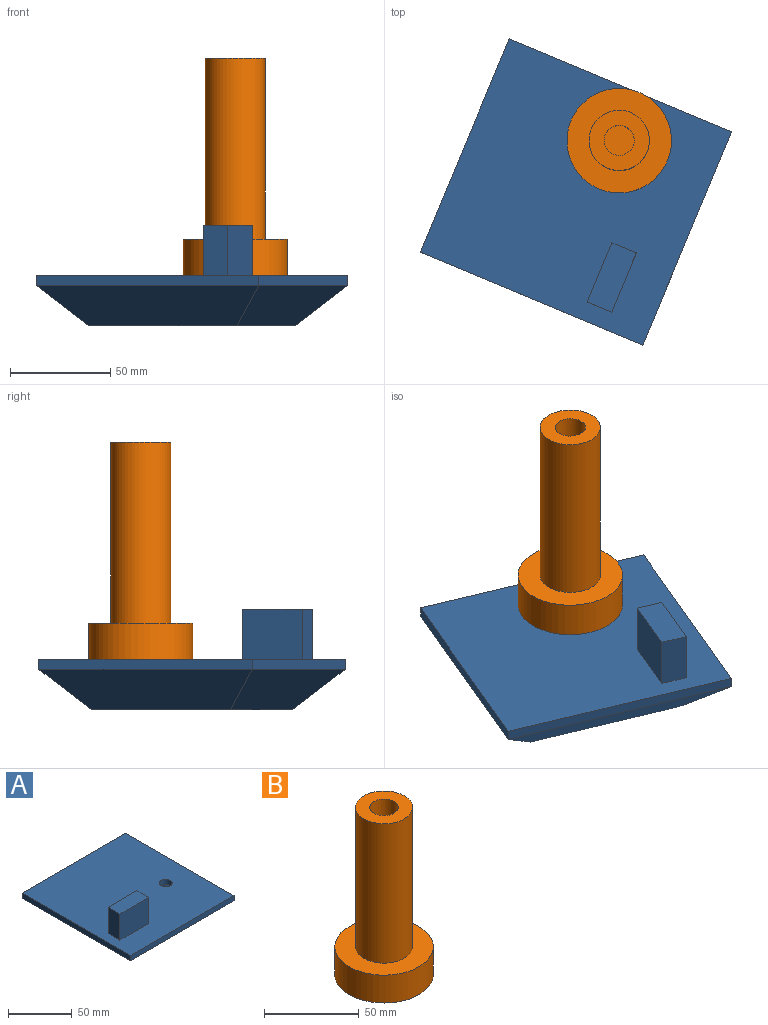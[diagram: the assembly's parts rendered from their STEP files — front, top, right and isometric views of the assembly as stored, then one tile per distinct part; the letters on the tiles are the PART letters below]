
ASSEMBLY  parts=2 mates=2
PART A: 17 faces, bbox 115x120x50 mm
  f0: plane 120x5mm, normal (-1,0,0), area 600mm2, adj f1,f4,f5,f12
  f1: plane 115x5mm, normal (0,-1,0), area 575mm2, adj f0,f2,f5,f15
  f2: plane 120x5mm, normal (1,0,0), area 600mm2, adj f1,f4,f5,f16
  f3: cylinder r=5mm len=10mm, axis (0,0,-1), area 157.1mm2, adj f5,f14
  f4: plane 115x5mm, normal (0,1,0), area 575mm2, adj f0,f2,f5,f13
  f5: plane 120x115mm, normal (0,0,1), area 13302.1mm2, adj f0,f1,f2,f3,f4,f7,f8,f9
  f6: plane 80x75mm, normal (0,0,-1), area 4736.5mm2, adj f12,f13,f14,f15,f16
  f7: plane 25x13.14mm, normal (-1,0,0), area 328.6mm2, adj f5,f8,f10,f11
  f8: plane 31.91x25mm, normal (0,-1,0), area 797.7mm2, adj f5,f7,f9,f11
  f9: plane 25x13.14mm, normal (1,0,0), area 328.6mm2, adj f5,f8,f10,f11
  f10: plane 31.91x25mm, normal (0,1,0), area 797.7mm2, adj f5,f7,f9,f11
  f11: plane 31.91x13.14mm, normal (0,0,1), area 419.3mm2, adj f7,f8,f9,f10
  f12: plane 120x20mm, normal (-0.71,0,-0.71), area 2828.4mm2, adj f0,f6,f13,f15
  f13: plane 115x20mm, normal (0,0.71,-0.71), area 2687mm2, adj f4,f6,f12,f16
  f14: cone r=25mm half-angle=45deg, axis (0,0,-1), area 2119.1mm2, adj f3,f6,f16
  f15: plane 115x20mm, normal (0,-0.71,-0.71), area 2687mm2, adj f1,f6,f12,f16
  f16: plane 120x20mm, normal (0.71,0,-0.71), area 2385.1mm2, adj f2,f6,f13,f14,f15
PART B: 7 faces, bbox 52x52x108 mm
  f0: cylinder r=26mm len=52mm, axis (0,0,-1), area 2940.5mm2, adj f1,f2
  f1: plane 52x52mm, normal (0,0,1), area 1416.9mm2, adj f0,f4
  f2: plane 52x52mm, normal (0,0,-1), area 2123.7mm2, adj f0
  f3: cylinder r=7.5mm len=90mm, axis (0,0,-1), area 4241.2mm2, adj f5,f6
  f4: cylinder r=15mm len=90mm, axis (0,0,-1), area 8482.3mm2, adj f1,f5
  f5: plane 30x30mm, normal (0,0,1), area 530.1mm2, adj f3,f4
  f6: plane 15x15mm, normal (0,0,1), area 176.7mm2, adj f3
PLACE A rot(axis=(0,0,1),67.3deg) t=(20.27,33.99,35.05)mm
PLACE B t=(6.79,1.7,60.05)mm fixed
MATE planar A.f5 <-> B.f0  axis (0,0,1) through (-15.39,-22.62,60.05)mm
MATE revolute A.f3 <-> B.f0  axis (0,0,1) through (6.79,1.7,60.05)mm
